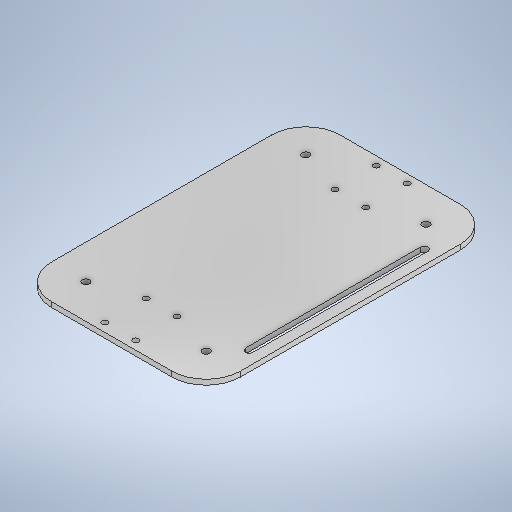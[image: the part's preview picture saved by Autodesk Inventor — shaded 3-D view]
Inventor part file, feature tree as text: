
AUTODESK INVENTOR PART (.ipt)
format: ipt  version: 2025.2 (Build 292293000, 293)  size: 303,104 bytes
history: native  units: mm
features: sketch x3, plane x3, extrude x2, hole x2, fillet x1
ambient origin geometry x8: Origin, YZ Plane, XZ Plane, XY Plane, X Axis, Y Axis, Z Axis, Center Point
bodies: Solid1 (feature_tree)
feature tree (11):
  sketch  "Sketch1"  dims[d4=110.0mm d5=168.0mm]
  extrude  "Extrusion2"  Depth=168.0mm
  hole  "Hole1"  [1 undecoded]
  fillet  "Fillet1"  Radius=18.0mm
  plane  "Work Plane1"
  plane  "Work Plane2"
  hole  "Hole2"  [1 undecoded]
  extrude  "Extrusion3"  Depth=4.3mm
  plane  "Work Plane3"
  sketch  "Sketch2"  dims[d20=3.0mm d21=0.0mm d22=5.0mm d23=18.0mm]
  sketch  "Sketch4"  dims[d24=24.0mm d25=5.0mm d26=18.0mm d27=24.0mm d28=3.4mm d29=6.0mm d30=4.0mm d31=2.0mm d32=90.0deg d33=8.0mm d34=20.594885mm d35=20.0mm d36=-84.0mm d37=-55.0mm d38=4.3mm d39=6.0mm d40=4.0mm d41=2.0mm d42=90.0deg d43=8.0mm d44=20.594885mm d45=8.0mm d46=102.0mm d47=8.0mm d48=4.3mm d49=0.0mm d50=0.0mm]
note: 2 required parameter values undecoded (feature->parameter linkage not recoverable at this tier; creation-order binding heuristic only, values carry confidence <= 0.55)
